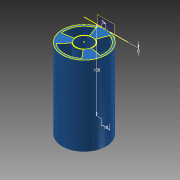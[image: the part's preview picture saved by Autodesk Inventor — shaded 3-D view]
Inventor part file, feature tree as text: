
AUTODESK INVENTOR PART (.ipt)
format: ipt  version: 2013 (Build 170138000, 138)  size: 203,264 bytes
history: native  units: mm
features: sketch x11, extrude x6, other x2, thread x2, hole x1
ambient origin geometry x8: Origin, YZ Plane, XZ Plane, XY Plane, X Axis, Y Axis, Z Axis, Center Point
feature tree (22):
  other  "ソリッド1"
  extrude  "押し出し1"  Depth=55.0mm
  extrude  "押し出し2"  Depth=100.0mm TaperAngle=0.0deg
  extrude  "押し出し3"  Depth=50.0mm
  extrude  "押し出し4"  Depth=97.0mm TaperAngle=0.0deg
  extrude  "押し出し5"  Depth=21.0mm
  sketch  "スケッチ6"
  other  "作業平面1"
  sketch  "スケッチ7"
  extrude  "押し出し6"  Depth=22.0mm
  hole  "穴1"  [1 undecoded]
  thread  "ねじ1"
  thread  "ねじ2"
  sketch  "スケッチ10"
  sketch  "スケッチ11"
  sketch  "スケッチ1"
  sketch  "スケッチ2"
  sketch  "スケッチ3"
  sketch  "スケッチ4"
  sketch  "スケッチ5"
  sketch  "スケッチ8"
  sketch  "スケッチ9"
note: 1 required parameter value undecoded (feature->parameter linkage not recoverable at this tier; creation-order binding heuristic only, values carry confidence <= 0.55)
